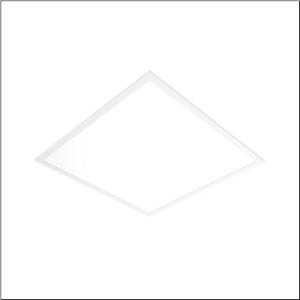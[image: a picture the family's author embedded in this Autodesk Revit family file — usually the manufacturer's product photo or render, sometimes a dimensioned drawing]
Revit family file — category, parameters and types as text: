
# Revit family: apollon_r__41_51mh11w72n43_7a0e
name_source: partatom
category: Lighting Fixtures
units: mm (PartAtom-declared; Revit-internal decimal feet)

## family parameters
Cut with Voids When Loaded = No
Host = Face
Light Source = No
Part Type = Normal
Room Calculation Point = No
Round Connector Dimension = Use Diameter
Shared = No

## types (1)
- --- (1 x LED, 3600 lm, 28.5 W, 6500K)
    Apparent Load = 29 VA
    CIE Flux Codes = 61 87 97 100 100
    Color Rendering = 80
    Color Temperature = 6500K
    Default Elevation = 1800 mm
    Description = Apollon® 41, office luminaire, primary optical cover: prismatic diffuser, of PS, light emission: direct distribution, primary light characteristic: symmetric, installation type: lay-in mounting, LED, rated luminous flux: 3.700lm, luminous efficacy: 130lm/W, light colour: 840/865, colour temperature: 4000/6500K, with terminal, 3-pole, mains connection: 220..240V, AC, 50/60Hz, housing, of aluminium section, traffic white (RAL 9016), module: M625, length: 620mm, width: 620mm, height: 28mm, housing upper side, of sheet steel, protection rating (complete): IP20, protection rating (lamp compartment, on room side): IP40, insulation class (complete): insulation class II (safety insulation), certification: CE, ENEC, permissible operating ambient temperature: -25..+40°C, packaging unit: 1 piece
    Height = 0 mm  [stored 0 ft]
    Lamp = 1 x LED
    Lamp Light Flux = 3600 lm
    Lamp Power = 28.5 W
    Lamp count = 1
    Length = 620 mm
    Luminous efficacy = 126 lm/W
    Manufacturer = Siteco
    ModVariant = No
    Model = 51MH11W72N43
    Mounting Place = Ceiling
    Mounting Type = Recessed
    Number of Poles = 1
    OnlyDefault = Yes
    Power Factor = 1
    Product Name = Apollon® 41
    Product group = office luminaire | ceiling recessed
    ProductGroupID = 401
    Protection Class = Protection class II
    Protection Degree = IP 20
    RLX_Detail_Level = 1
    RLX_Emergency_Light_Flux = 0 lm
    RLX_Emergency_Type = 0
    RLX_Emergency_Type_DB = No
    RlxData = <blob elided: 12405 chars, md5=45437990>
    Socket = socket
    Standby Power = 0 W
    System Light Flux = 3600 lm
    System Power = 29 W
    Type Comments = individual setting
    Type Image = l_1291024.jpg
    URL = http://relux.com
    VarID = @adj_027747
    Voltage = 0 V
    Weight = 0.00 kg
    Width = 620 mm

note: [stored X ft] marks values corroborated as IEEE doubles in the binary element streams (Revit-internal decimal feet)

## geometry (parser evidence)
native form markers: Sweep x9
no freeform markers — native parametric forms only
